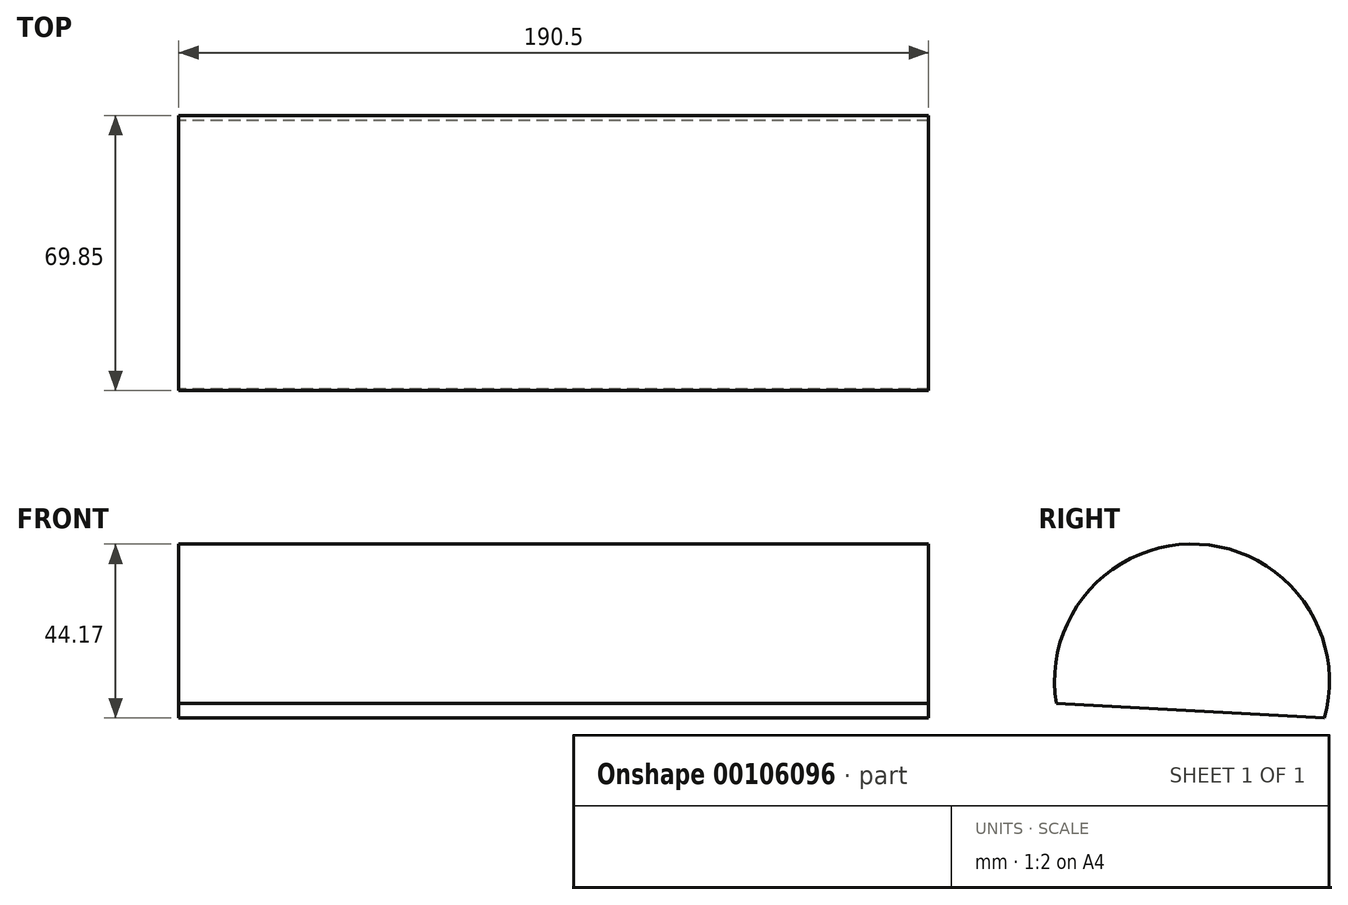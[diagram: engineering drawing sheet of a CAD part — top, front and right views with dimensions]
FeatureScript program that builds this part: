
annotation { "Feature Type Name" : "Feature", "Feature Type Description" : "" }
export const myFeature = defineFeature(function(context is Context, id is Id, definition is map)
    precondition{}
    {
        {
            var Q0;
            Q0=qCreatedBy(makeId("Right.planeOp"),FACE);
            var sketch = newSketch(context, id + "F0", { "sketchPlane" : qUnion([Q0])});
            skArc(sketch, "E0", {"start": v(14.18, 0) * mm, "mid": v(-17.64, 44.12) * mm, "end": v(-53.96, 3.62) * mm});
            skLineSegment(sketch, "E1", {"start": v(-53.96, 3.62) * mm, "end": v(14.18, 0) * mm});
            skSolve(sketch);
        }
        {
            var Q0;
            Q0=makeQuery(id+"F0.imprint","IMPRINT",FACE,{"disambiguationData":[TD([[makeQuery(id+"F0.imprint","IMPRINT",EDGE,{"derivedFrom":sQuery(id+"F0.wireOp",EDGE,"E0")}),1.0]])]});
            extrude(context, id + "F1", {"entities" : qUnion([Q0]), "depth" : 190.5 * mm});
        }
    });
